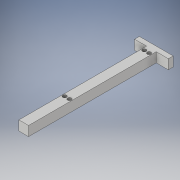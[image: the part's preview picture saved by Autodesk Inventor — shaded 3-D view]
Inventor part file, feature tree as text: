
AUTODESK INVENTOR PART (.ipt)
format: ipt  version: 2017.3 (Build 213256000, 256)  size: 111,616 bytes
history: native  units: in
note: dims shown in document units (in); Inventor stores cm internally (conversion verified against a paired STEP export)
features: sketch x3, extrude x2, hole x1
ambient origin geometry x8: Origin, YZ Plane, XZ Plane, XY Plane, X Axis, Y Axis, Z Axis, Center Point
bodies: Solid1 (feature_tree)
feature tree (6):
  extrude  "Extrusion1"  Depth=0.25in
  extrude  "Extrusion2"  Depth=0.25in
  hole  "Hole1"  [1 undecoded]
  sketch  "Sketch1"  dims[d0=0.875in d1=0.25in]
  sketch  "Sketch2"  dims[d2=0.125in d3=0.0in d4=0.25in]
  sketch  "Sketch3"  dims[d5=3.312in d6=0.0in d7=0.098in d8=0.25in d9=0.375in d10=0.25in d11=0.5635in d12=0.375in d13=0.8108in]
note: 1 required parameter value undecoded (feature->parameter linkage not recoverable at this tier; creation-order binding heuristic only, values carry confidence <= 0.55)
